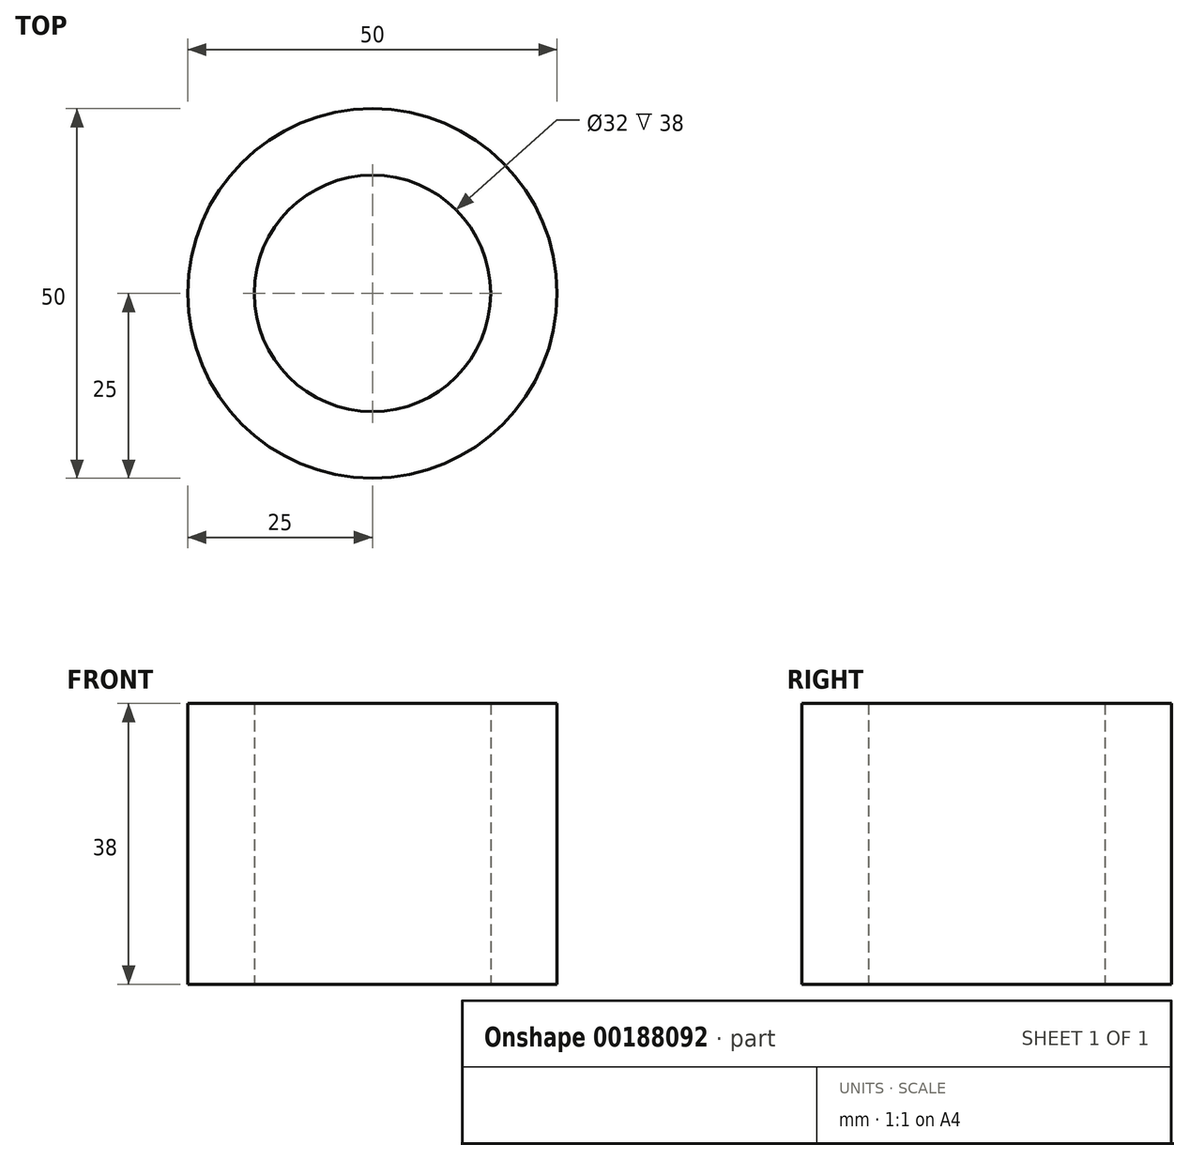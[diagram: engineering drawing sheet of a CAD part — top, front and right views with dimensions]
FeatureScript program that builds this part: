
annotation { "Feature Type Name" : "Feature", "Feature Type Description" : "" }
export const myFeature = defineFeature(function(context is Context, id is Id, definition is map)
    precondition{}
    {
        {
            var Q0;
            Q0=qCreatedBy(makeId("Top.planeOp"),FACE);
            var sketch = newSketch(context, id + "F0", { "sketchPlane" : qUnion([Q0])});
            skCircle(sketch, "E0", {"center": v(0, 0) * mm, "radius": 25 * mm});
            skCircle(sketch, "E1", {"center": v(0, 0) * mm, "radius": 16 * mm});
            skSolve(sketch);
        }
        {
            var Q0;
            Q0 = qSketchRegion(id + "F0", true);
            extrude(context, id + "F1", {"entities" : qUnion([Q0]), "depth" : 38 * mm});
        }
    });
